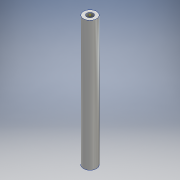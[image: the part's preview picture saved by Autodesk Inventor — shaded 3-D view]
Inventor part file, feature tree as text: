
AUTODESK INVENTOR PART (.ipt)
format: ipt  version: 2016 (Build 200138000, 138)  size: 100,352 bytes
history: native  units: mm
features: sketch x3, other x2, extrude x2
ambient origin geometry x8: Origin, YZ Plane, XZ Plane, XY Plane, X Axis, Y Axis, Z Axis, Center Point
bodies: Body1 (feature_tree)
feature tree (7):
  other  "ソリッド1"
  extrude  "押し出し1"  Depth=6.0mm
  sketch  "スケッチ2"
  other  "作業平面1"
  extrude  "押し出し2"  Depth=3.0mm
  sketch  "スケッチ1"
  sketch  "スケッチ3"
